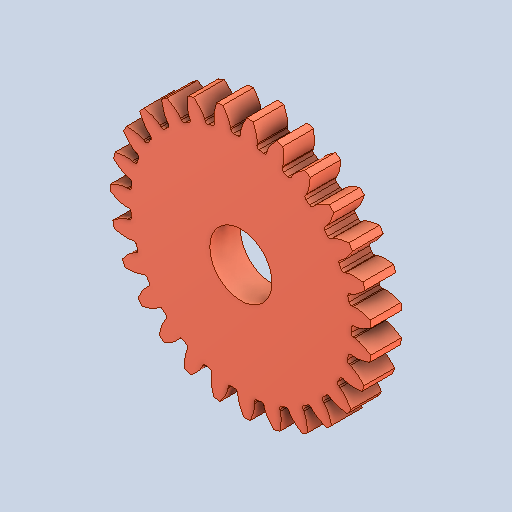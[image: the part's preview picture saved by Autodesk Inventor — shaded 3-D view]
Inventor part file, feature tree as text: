
AUTODESK INVENTOR PART (.ipt)
format: ipt  version: 2022 (Build 260153000, 153)  size: 458,240 bytes
history: imported  units: in
note: dims shown in document units (in); Inventor stores cm internally (conversion verified against a paired STEP export)
features: imported_body x1
ambient origin geometry x8: Origin, YZ Plane, XZ Plane, XY Plane, X Axis, Y Axis, Z Axis, Center Point
bodies: Solid1 (imported_parasolid), Body1 (imported_parasolid)
feature tree (1):
  imported_body  NMx_Import_Brep_tag  [imported B-rep: ~17 faces, bbox_mm=[8.277971, 8.292544, 3.1242]]
